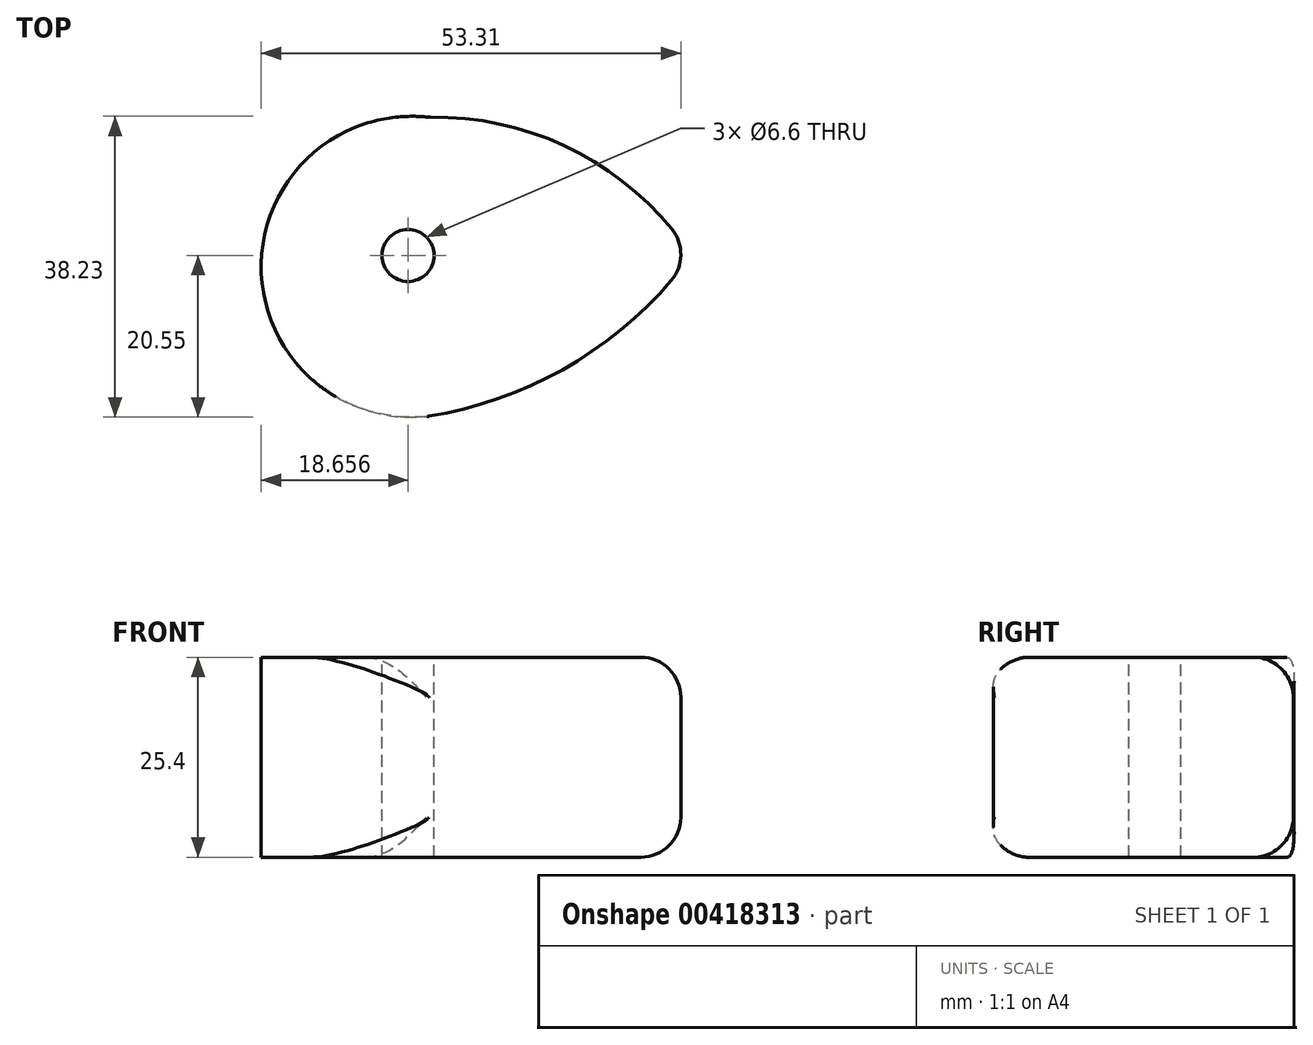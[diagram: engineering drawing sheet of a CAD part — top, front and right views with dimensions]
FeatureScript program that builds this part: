
annotation { "Feature Type Name" : "Feature", "Feature Type Description" : "" }
export const myFeature = defineFeature(function(context is Context, id is Id, definition is map)
    precondition{}
    {
        {
            var Q0;
            Q0=qCreatedBy(makeId("Top.planeOp"),FACE);
            var sketch = newSketch(context, id + "F0", { "sketchPlane" : qUnion([Q0])});
            skArc(sketch, "E0", {"start": v(0, 17.56) * mm, "mid": v(-21.22, -1.44) * mm, "end": v(0, -20.43) * mm});
            skArc(sketch, "E1", {"start": v(33.39, 0) * mm, "mid": v(18.97, 13.1) * mm, "end": v(0, 17.56) * mm});
            skArc(sketch, "E2", {"start": v(0, -20.43) * mm, "mid": v(18.73, -13.54) * mm, "end": v(33.39, 0) * mm});
            skSolve(sketch);
        }
        {
            var Q0;
            Q0 = qSketchRegion(id + "F0", true);
            extrude(context, id + "F1", {"entities" : qUnion([Q0]), "depth" : 25.4 * mm});
        }
        {
            var Q0;
            Q0=makeQuery(id+"F1.opExtrude","SWEPT_FACE",FACE,{"disambiguationData":[OSD([sQuery(id+"F0.wireOp",EDGE,"E2")])]});
            var Q1;
            Q1=makeQuery(id+"F1.opExtrude","SWEPT_FACE",FACE,{"disambiguationData":[OSD([sQuery(id+"F0.wireOp",EDGE,"E1")])]});
            fillet(context, id + "F2", {"entities" : qUnion([Q0, Q1]), "radius" : 5.08 * mm, "tangentPropagation" : true, "allowEdgeOverflow" : false});
        }
        {
            var Q0;
            Q0=makeQuery(id+"F1.opExtrude","CAP_FACE",FACE,{"disambiguationData":[OSD([sQuery(id+"F0.wireOp",EDGE,"E0"),sQuery(id+"F0.wireOp",EDGE,"E1"),sQuery(id+"F0.wireOp",EDGE,"E2")])],"isStart":false});
            var sketch = newSketch(context, id + "F3", { "sketchPlane" : qUnion([Q0])});
            skCircle(sketch, "E3", {"center": v(-2.56, 0) * mm, "radius": 3.3 * mm});
            skSolve(sketch);
        }
        {
            var Q0;
            Q0 = qSketchRegion(id + "F3", true);
            extrude(context, id + "F4", {"entities" : qUnion([Q0]), "operationType" : NewBodyOperationType.REMOVE, "oppositeDirection" : true, "depth" : 25.4 * mm});
        }
    });
